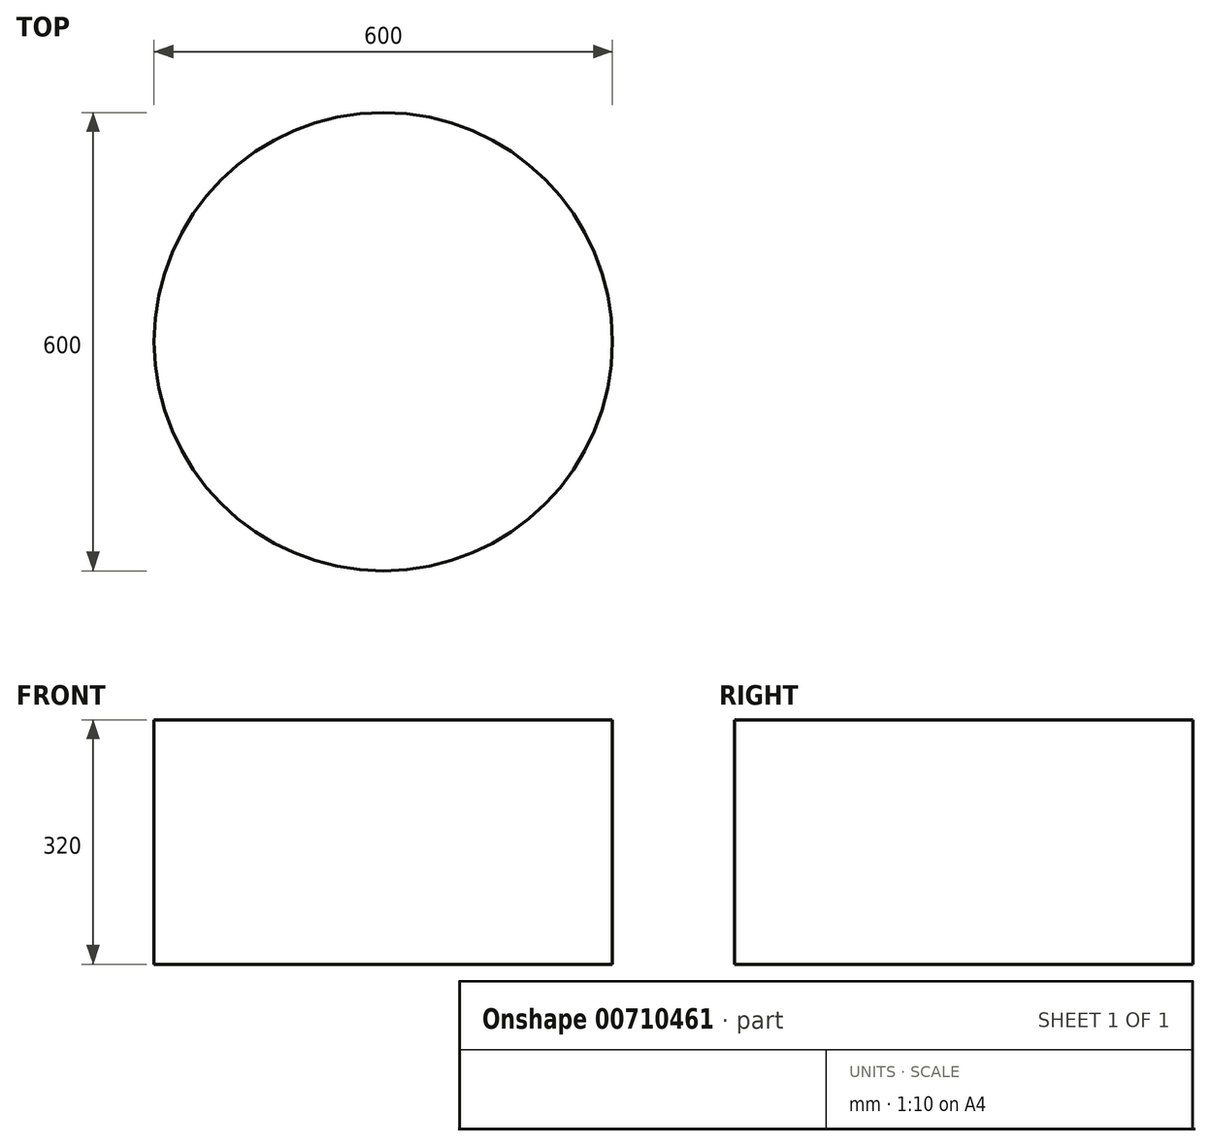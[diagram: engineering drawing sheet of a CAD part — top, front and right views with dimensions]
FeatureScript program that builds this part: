
annotation { "Feature Type Name" : "Feature", "Feature Type Description" : "" }
export const myFeature = defineFeature(function(context is Context, id is Id, definition is map)
    precondition{}
    {
        {
            var Q0;
            Q0=qCreatedBy(makeId("Top.planeOp"),FACE);
            var sketch = newSketch(context, id + "F0", { "sketchPlane" : qUnion([Q0])});
            skCircle(sketch, "E0", {"center": v(0, 0) * mm, "radius": 300 * mm});
            skSolve(sketch);
        }
        {
            var Q0;
            Q0=makeQuery(id+"F0.imprint","IMPRINT",FACE,{"disambiguationData":[TD([[makeQuery(id+"F0.imprint","IMPRINT",EDGE,{"derivedFrom":sQuery(id+"F0.wireOp",EDGE,"E0")}),1.0]])]});
            extrude(context, id + "F1", {"entities" : qUnion([Q0]), "depth" : 320 * mm, "offsetDistance" : 25 * mm});
        }
    });
